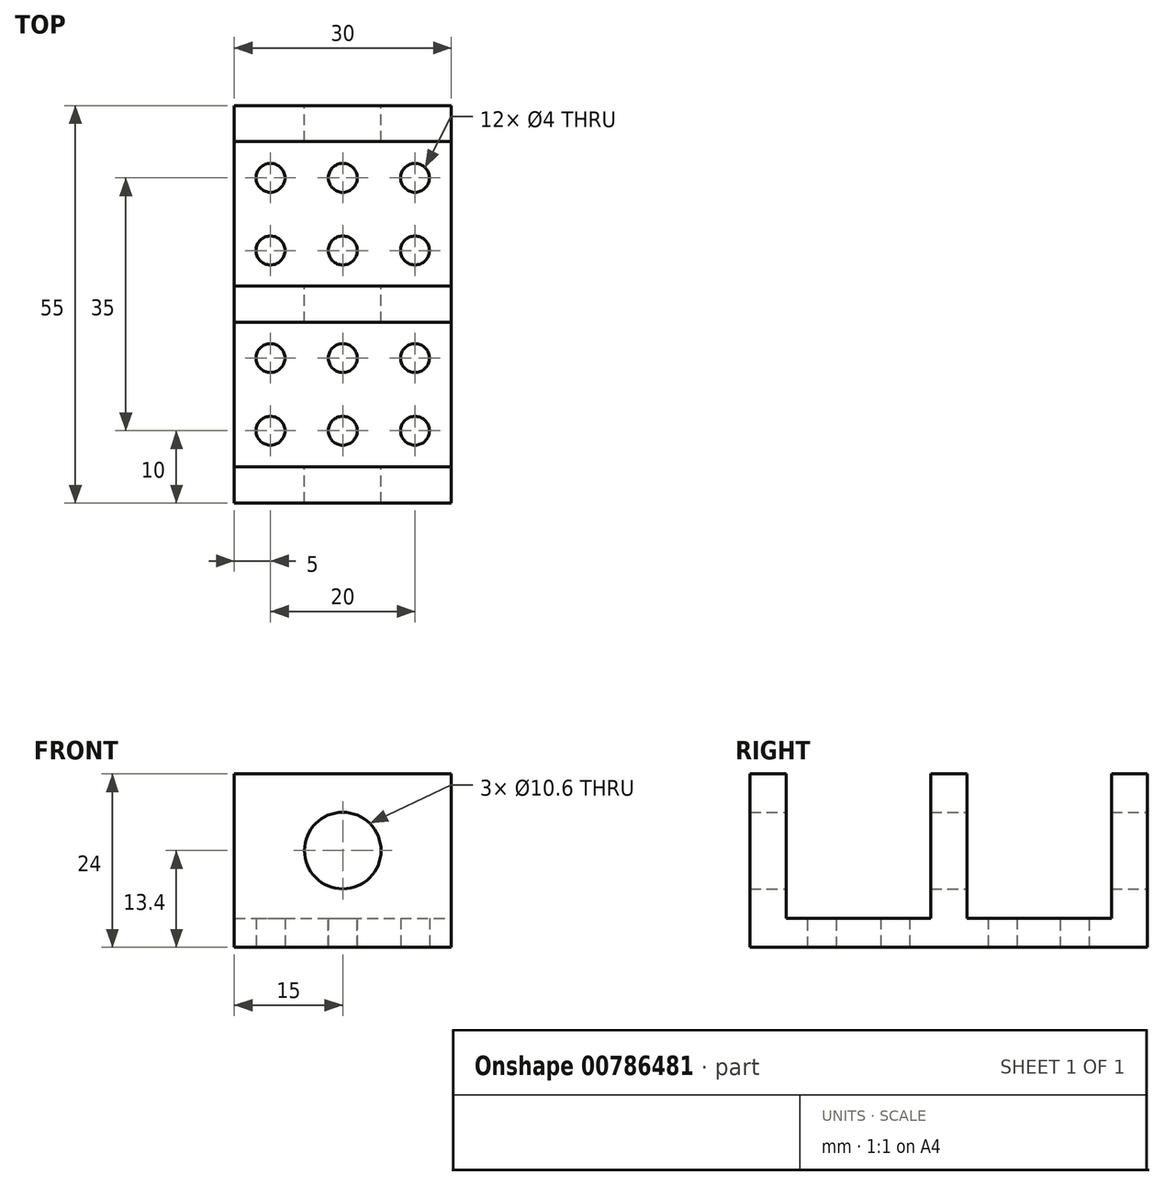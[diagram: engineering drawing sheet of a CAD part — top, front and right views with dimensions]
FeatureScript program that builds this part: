
annotation { "Feature Type Name" : "Feature", "Feature Type Description" : "" }
export const myFeature = defineFeature(function(context is Context, id is Id, definition is map)
    precondition{}
    {
        {
            var Q0;
            Q0=qCreatedBy(makeId("Top.planeOp"),FACE);
            var sketch = newSketch(context, id + "F0", { "sketchPlane" : qUnion([Q0])});
            skLineSegment(sketch, "E0.bottom", {"start": v(-15, 27.5) * mm, "end": v(15, 27.5) * mm});
            skLineSegment(sketch, "E0.top", {"start": v(-15, -27.5) * mm, "end": v(15, -27.5) * mm});
            skLineSegment(sketch, "E0.left", {"start": v(-15, 27.5) * mm, "end": v(-15, -27.5) * mm});
            skLineSegment(sketch, "E0.right", {"start": v(15, 27.5) * mm, "end": v(15, -27.5) * mm});
            skSolve(sketch);
        }
        {
            var Q0;
            Q0 = qSketchRegion(id + "F0", true);
            extrude(context, id + "F1", {"entities" : qUnion([Q0]), "depth" : 4 * mm, "offsetDistance" : 25 * mm});
        }
        {
            var Q0;
            Q0=makeQuery(id+"F1.opExtrude","CAP_FACE",FACE,{"disambiguationData":[OSD([sQuery(id+"F0.wireOp",EDGE,"E0.bottom"),sQuery(id+"F0.wireOp",EDGE,"E0.top"),sQuery(id+"F0.wireOp",EDGE,"E0.left"),sQuery(id+"F0.wireOp",EDGE,"E0.right")])],"isStart":false});
            var sketch = newSketch(context, id + "F2", { "sketchPlane" : qUnion([Q0])});
            skCircle(sketch, "E1", {"center": v(0, -17.5) * mm, "radius": 2 * mm});
            skCircle(sketch, "E2", {"center": v(0, 17.5) * mm, "radius": 2 * mm});
            skSolve(sketch);
        }
        {
            var Q0;
            Q0 = qSketchRegion(id + "F2", true);
            extrude(context, id + "F3", {"entities" : qUnion([Q0]), "operationType" : NewBodyOperationType.REMOVE, "oppositeDirection" : true, "depth" : 4 * mm, "offsetDistance" : 25 * mm});
        }
        {
            var Q0;
            Q0=makeQuery(id+"F1.opExtrude","CAP_FACE",FACE,{"disambiguationData":[OSD([sQuery(id+"F0.wireOp",EDGE,"E0.bottom"),sQuery(id+"F0.wireOp",EDGE,"E0.top"),sQuery(id+"F0.wireOp",EDGE,"E0.left"),sQuery(id+"F0.wireOp",EDGE,"E0.right")])],"isStart":false});
            var sketch = newSketch(context, id + "F4", { "sketchPlane" : qUnion([Q0])});
            skLineSegment(sketch, "E3.bottom", {"start": v(-15, 27.5) * mm, "end": v(15, 27.5) * mm});
            skLineSegment(sketch, "E3.top", {"start": v(-15, 22.5) * mm, "end": v(15, 22.5) * mm});
            skLineSegment(sketch, "E3.left", {"start": v(-15, 27.5) * mm, "end": v(-15, 22.5) * mm});
            skLineSegment(sketch, "E3.right", {"start": v(15, 27.5) * mm, "end": v(15, 22.5) * mm});
            skLineSegment(sketch, "E4.bottom", {"start": v(-15, 2.5) * mm, "end": v(15, 2.5) * mm});
            skLineSegment(sketch, "E4.top", {"start": v(-15, -2.5) * mm, "end": v(15, -2.5) * mm});
            skLineSegment(sketch, "E4.left", {"start": v(-15, 2.5) * mm, "end": v(-15, -2.5) * mm});
            skLineSegment(sketch, "E4.right", {"start": v(15, 2.5) * mm, "end": v(15, -2.5) * mm});
            skLineSegment(sketch, "E5.bottom", {"start": v(-15, -27.5) * mm, "end": v(15, -27.5) * mm});
            skLineSegment(sketch, "E5.top", {"start": v(-15, -22.5) * mm, "end": v(15, -22.5) * mm});
            skLineSegment(sketch, "E5.left", {"start": v(-15, -27.5) * mm, "end": v(-15, -22.5) * mm});
            skLineSegment(sketch, "E5.right", {"start": v(15, -27.5) * mm, "end": v(15, -22.5) * mm});
            skSolve(sketch);
        }
        {
            var Q0;
            Q0 = qSketchRegion(id + "F4", true);
            extrude(context, id + "F5", {"entities" : qUnion([Q0]), "operationType" : NewBodyOperationType.ADD, "depth" : 20 * mm, "offsetDistance" : 25 * mm});
        }
        {
            var Q0;
            Q0=makeQuery(id+"F5.boolean.opBoolean","MERGE",FACE,{"derivedFrom":[makeQuery(id+"F1.opExtrude","SWEPT_FACE",FACE,{"disambiguationData":[OSD([sQuery(id+"F0.wireOp",EDGE,"E0.bottom")])]}),makeQuery(id+"F5.opExtrude","SWEPT_FACE",FACE,{"disambiguationData":[OSD([sQuery(id+"F4.wireOp",EDGE,"E3.bottom")])]})]});
            var sketch = newSketch(context, id + "F6", { "sketchPlane" : qUnion([Q0])});
            skCircle(sketch, "E6", {"center": v(0, 13.4) * mm, "radius": 5.3 * mm});
            skSolve(sketch);
        }
        {
            var Q0;
            Q0 = qSketchRegion(id + "F6", true);
            extrude(context, id + "F7", {"entities" : qUnion([Q0]), "operationType" : NewBodyOperationType.REMOVE, "endBound" : BoundingType.THROUGH_ALL, "oppositeDirection" : true, "depth" : 25 * mm, "offsetDistance" : 25 * mm});
        }
        {
            var Q0;
            Q0=makeQuery(id+"F1.opExtrude","CAP_FACE",FACE,{"disambiguationData":[OSD([sQuery(id+"F0.wireOp",EDGE,"E0.bottom"),sQuery(id+"F0.wireOp",EDGE,"E0.top"),sQuery(id+"F0.wireOp",EDGE,"E0.left"),sQuery(id+"F0.wireOp",EDGE,"E0.right")])],"isStart":true});
            var sketch = newSketch(context, id + "F8", { "sketchPlane" : qUnion([Q0])});
            skCircle(sketch, "E7", {"center": v(10, -17.5) * mm, "radius": 2 * mm});
            skCircle(sketch, "E8", {"center": v(10, -7.45) * mm, "radius": 2 * mm});
            skCircle(sketch, "E9.MirrorC", {"center": v(-10, -17.5) * mm, "radius": 2 * mm});
            skCircle(sketch, "E10.MirrorC", {"center": v(-10, -7.45) * mm, "radius": 2 * mm});
            skCircle(sketch, "E11.MirrorC", {"center": v(-10, 7.45) * mm, "radius": 2 * mm});
            skCircle(sketch, "E12.MirrorC", {"center": v(-10, 17.5) * mm, "radius": 2 * mm});
            skCircle(sketch, "E13.MirrorC", {"center": v(10, 17.5) * mm, "radius": 2 * mm});
            skCircle(sketch, "E14.MirrorC", {"center": v(10, 7.45) * mm, "radius": 2 * mm});
            skCircle(sketch, "E15", {"center": v(0, -7.45) * mm, "radius": 2 * mm});
            skCircle(sketch, "E16", {"center": v(0, 7.45) * mm, "radius": 2 * mm});
            skSolve(sketch);
        }
        {
            var Q0;
            Q0 = qSketchRegion(id + "F8", true);
            extrude(context, id + "F9", {"entities" : qUnion([Q0]), "operationType" : NewBodyOperationType.REMOVE, "oppositeDirection" : true, "depth" : 4 * mm, "offsetDistance" : 25 * mm});
        }
    });
